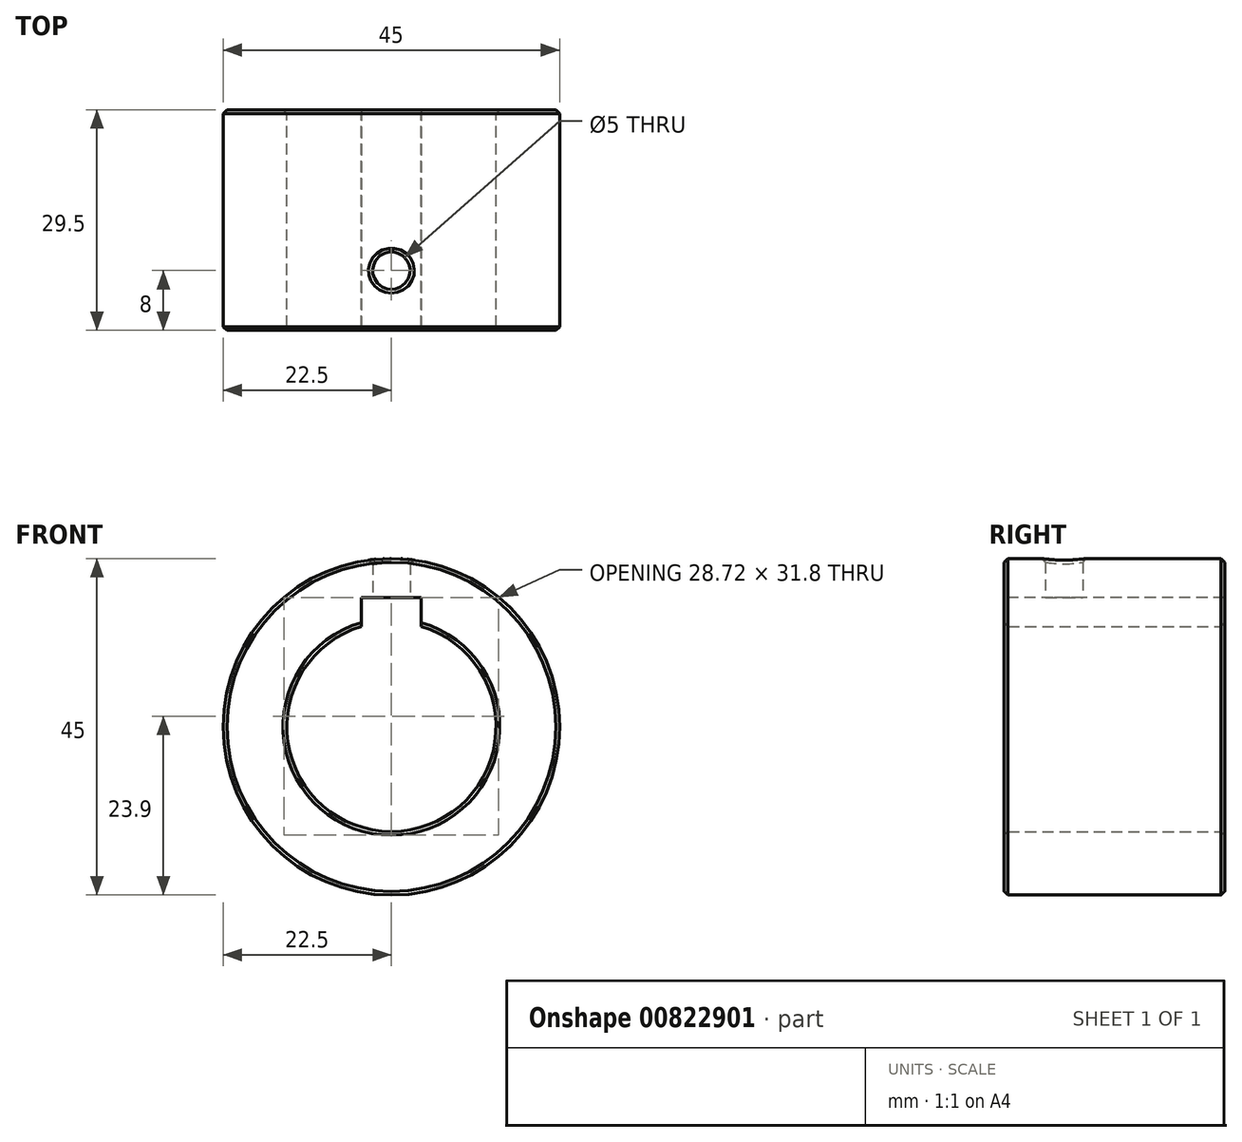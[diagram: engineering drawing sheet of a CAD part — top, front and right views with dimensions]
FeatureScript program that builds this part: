
annotation { "Feature Type Name" : "Feature", "Feature Type Description" : "" }
export const myFeature = defineFeature(function(context is Context, id is Id, definition is map)
    precondition{}
    {
        {
            var Q0;
            Q0=qCreatedBy(makeId("Front.planeOp"),FACE);
            var sketch = newSketch(context, id + "F0", { "sketchPlane" : qUnion([Q0])});
            skCircle(sketch, "E0", {"center": v(0, 0) * mm, "radius": 14 * mm});
            skCircle(sketch, "E1", {"center": v(0, 0) * mm, "radius": 22.5 * mm});
            skLineSegment(sketch, "E2", {"start": v(0, 0) * mm, "end": v(22.5, 0) * mm, "construction": true});
            skLineSegment(sketch, "E3.1.0", {"start": v(0, 0) * mm, "end": v(0, 22.5) * mm, "construction": true});
            skLineSegment(sketch, "E3.2.0", {"start": v(0, 0) * mm, "end": v(-22.5, 0) * mm, "construction": true});
            skLineSegment(sketch, "E3.3.0", {"start": v(0, 0) * mm, "end": v(0, -22.5) * mm, "construction": true});
            skSolve(sketch);
        }
        {
            var Q0;
            Q0 = qSketchRegion(id + "F0", true);
            extrude(context, id + "F1", {"entities" : qUnion([Q0]), "depth" : 29.5 * mm, "offsetDistance" : 25 * mm});
        }
        {
            var Q0;
            Q0=makeQuery(id+"F1.opExtrude","SWEPT_FACE",FACE,{"disambiguationData":[OSD([sQuery(id+"F0.wireOp",EDGE,"E0")])]});
            var Q1;
            Q1=makeQuery(id+"F1.opExtrude","SWEPT_FACE",FACE,{"disambiguationData":[OSD([sQuery(id+"F0.wireOp",EDGE,"E1")])]});
            chamfer(context, id + "F2", {"entities" : qUnion([Q0, Q1]), "width" : 0.5 * mm, "tangentPropagation" : true});
        }
        {
            var Q0;
            Q0=makeQuery(id+"F1.opExtrude","CAP_FACE",FACE,{"disambiguationData":[OSD([sQuery(id+"F0.wireOp",EDGE,"E0"),sQuery(id+"F0.wireOp",EDGE,"E1")])],"isStart":false});
            var sketch = newSketch(context, id + "F3", { "sketchPlane" : qUnion([Q0])});
            skCircle(sketch, "E4.0", {"center": v(0, 0) * mm, "radius": 14 * mm, "construction": true});
            skLineSegment(sketch, "E5", {"start": v(0, 0) * mm, "end": v(0, 13.8) * mm, "construction": true});
            skLineSegment(sketch, "E6.bottom", {"start": v(4, 17.3) * mm, "end": v(-4, 17.3) * mm});
            skLineSegment(sketch, "E6.top", {"start": v(4, 10.3) * mm, "end": v(-4, 10.3) * mm});
            skLineSegment(sketch, "E6.left", {"start": v(4, 17.3) * mm, "end": v(4, 10.3) * mm});
            skLineSegment(sketch, "E6.right", {"start": v(-4, 17.3) * mm, "end": v(-4, 10.3) * mm});
            skPoint(sketch, "E6.middle", {"position": v(0, 13.8) * mm});
            skPoint(sketch, "E7", {"position": v(0, -14) * mm});
            skSolve(sketch);
        }
        {
            var Q0;
            Q0 = qSketchRegion(id + "F3", true);
            extrude(context, id + "F4", {"entities" : qUnion([Q0]), "operationType" : NewBodyOperationType.REMOVE, "endBound" : BoundingType.UP_TO_NEXT, "oppositeDirection" : true, "depth" : 25 * mm, "offsetDistance" : 25 * mm});
        }
        {
            var Q0;
            Q0=qCreatedBy(makeId("Top.planeOp"),FACE);
            var sketch = newSketch(context, id + "F5", { "sketchPlane" : qUnion([Q0])});
            skLineSegment(sketch, "E8", {"start": v(0, 0) * mm, "end": v(0, -21.5) * mm, "construction": true});
            skCircle(sketch, "E9", {"center": v(0, -21.5) * mm, "radius": 2.5 * mm});
            skLineSegment(sketch, "E10.0", {"start": v(22, -29.5) * mm, "end": v(-22, -29.5) * mm, "construction": true});
            skPoint(sketch, "E11", {"position": v(0, -29.5) * mm});
            skSolve(sketch);
        }
        {
            var Q0;
            Q0 = qSketchRegion(id + "F5", true);
            extrude(context, id + "F6", {"entities" : qUnion([Q0]), "operationType" : NewBodyOperationType.REMOVE, "depth" : 25 * mm, "offsetDistance" : 25 * mm});
        }
        {
            var Q0;
            Q0=makeQuery(id+"F6.boolean.opBoolean","INTERSECT",EDGE,{"derivedFrom":[makeQuery(id+"F1.opExtrude","SWEPT_FACE",FACE,{"disambiguationData":[OSD([sQuery(id+"F0.wireOp",EDGE,"E1")])]}),makeQuery(id+"F6.opExtrude","SWEPT_FACE",FACE,{"disambiguationData":[OSD([sQuery(id+"F5.wireOp",EDGE,"E9")])]})]});
            chamfer(context, id + "F7", {"entities" : qUnion([Q0]), "width" : 0.5 * mm, "tangentPropagation" : true});
        }
    });
